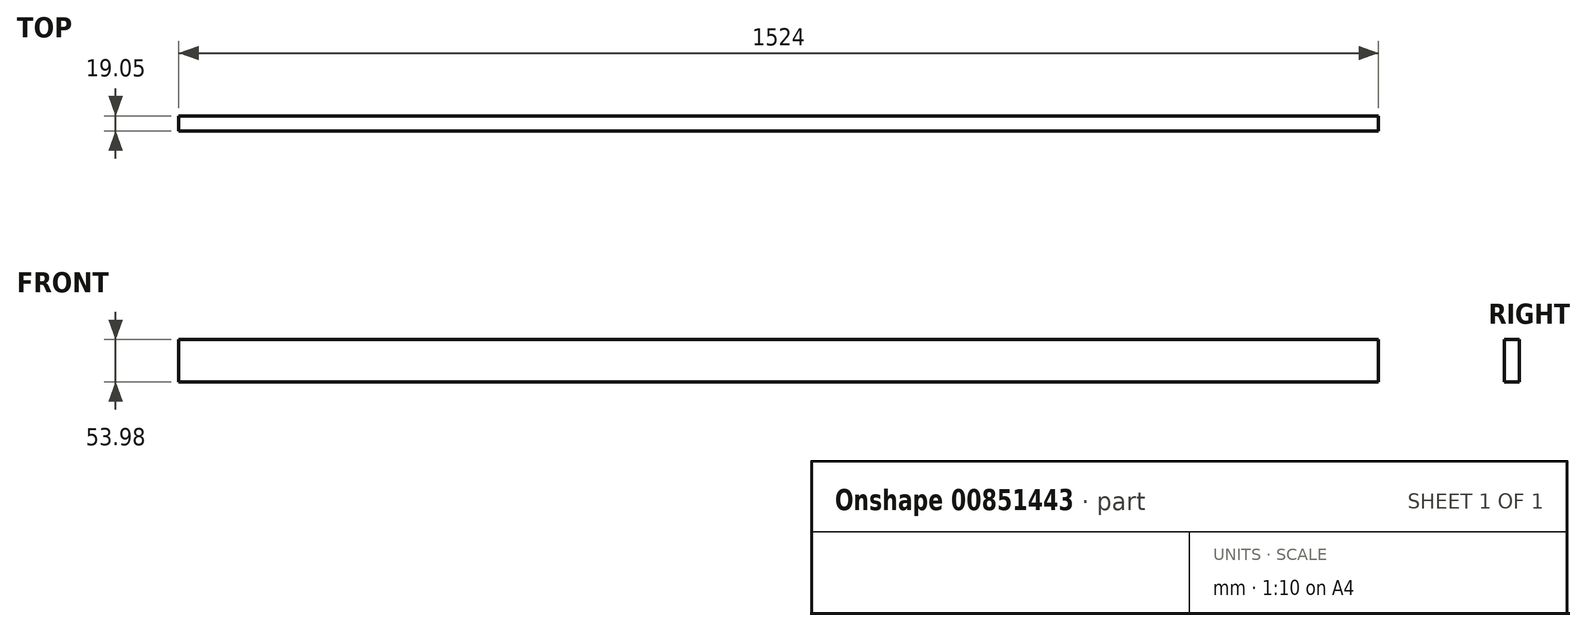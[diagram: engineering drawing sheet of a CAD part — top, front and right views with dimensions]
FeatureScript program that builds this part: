
annotation { "Feature Type Name" : "Feature", "Feature Type Description" : "" }
export const myFeature = defineFeature(function(context is Context, id is Id, definition is map)
    precondition{}
    {
        {
            var Q0;
            Q0=qCreatedBy(makeId("Front.planeOp"),FACE);
            var sketch = newSketch(context, id + "F0", { "sketchPlane" : qUnion([Q0])});
            skLineSegment(sketch, "E0", {"start": v(0, 0) * mm, "end": v(1524, 0) * mm});
            skLineSegment(sketch, "E1", {"start": v(0, 0) * mm, "end": v(0, 53.98) * mm});
            skLineSegment(sketch, "E2", {"start": v(0, 53.98) * mm, "end": v(1524, 53.98) * mm});
            skLineSegment(sketch, "E3", {"start": v(1524, 53.98) * mm, "end": v(1524, 0) * mm});
            skSolve(sketch);
        }
        {
            var Q0;
            Q0 = qSketchRegion(id + "F0", true);
            extrude(context, id + "F1", {"entities" : qUnion([Q0]), "depth" : 19.05 * mm, "offsetDistance" : 25.4 * mm});
        }
    });
